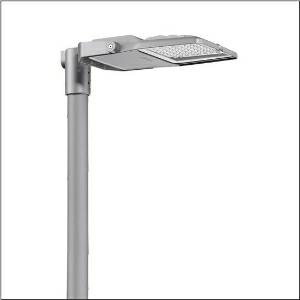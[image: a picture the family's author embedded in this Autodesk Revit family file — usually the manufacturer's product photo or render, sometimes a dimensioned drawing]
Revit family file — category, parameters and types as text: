
# Revit family: floodlight_fl_21_mini___pl43_5xa7772c4a3a_aec0
name_source: partatom
category: Lighting Fixtures
units: mm (PartAtom-declared; Revit-internal decimal feet)

## family parameters
Cut with Voids When Loaded = No
Host = Face
Light Source = No
Part Type = Normal
Room Calculation Point = No
Round Connector Dimension = Use Diameter
Shared = No

## types (1)
- --- (1 x LED, 13050 lm, 87.2 W, 4000K)
    Apparent Load = 87 VA
    CIE Flux Codes = 27 78 99 100 100
    Color Rendering = 70
    Color Temperature = 4000K
    Default Elevation = 1800 mm
    Description = Floodlight FL 21 mini, floodlight, primary light control with lens, of PMMA, primary optical cover: protective disc, of toughened safety glass, transparent, light distribution: PL43, light emission: direct distribution, installation type: surface-mounted, LED, High Power LED, rated luminous flux: 13.050lm, luminous efficacy: 150lm/W, light colour: 740, colour temperature: 4000K, control gear: ECG iQ, control: Auto-Match, Temp-Guard, Night-Set, Smart-Wire, Desk-Remote (wireless, voltage-free reading and setting of iQ features in the workshop via application-optimized NFC function/RFID function), optimised constant luminous flux control (CLO 2.0), Light-Fading, Lumen-Switch, with terminal, 6-pole, mains connection: 220..240V, AC, 50/60Hz, start of lifetime: 87W, end of lifetime: 92W, reduction: 40W, luminaire housing, of diecast aluminium, powder-coated, Siteco® metallic grey (DB 702S), corrosivity category C5 according to DIN EN ISO 12944, mast bracket, of steel, galvanised, powder-coated, protection rating (complete): IP66, insulation class (complete): insulation class II (safety insulation), certification: CE, ENEC, VDE, protection symbol: D, impact resistance: IK08, permissible operating ambient temperature: -40..+40°C, permissible operating ambient temperature for outdoor applications: -40..+50°C, standard: DIN EN 12944, packaging unit: 1 piece

Light Distribution: PL43
    Height = 70 mm
    Lamp = 1 x LED
    Lamp Light Flux = 13050 lm
    Lamp Power = 87.2 W
    Lamp count = 1
    Length = 485 mm
    Luminous efficacy = 150 lm/W
    Manufacturer = Siteco
    ModVariant = No
    Model = 5XA7772C4A3A
    Number of Poles = 1
    OnlyDefault = Yes
    Power Factor = 1
    Product Name = Floodlight FL 21 mini | PL43
    Product group = floodlight | pylon top
    ProductGroupID = 6101
    Protection Class = Protection class II
    Protection Degree = IP 66
    RLX_Detail_Level = 1
    RlxData = <blob elided: 101101 chars, md5=14559125>
    Socket = socket
    Standby Power = 0 W
    System Light Flux = 13050 lm
    System Power = 87 W
    Type Comments = factory setting: luminous flux: 100 % | dim-lin: 254 | 456 mA
    Type Image = l_1007125.jpg
    URL = http://relux.com
    VarID = @adj_073349
    Voltage = 0 V
    Weight = 0.00 kg
    Width = 337 mm

## geometry (parser evidence)
native form markers: Blend x4, Sweep x12
no freeform markers — native parametric forms only
